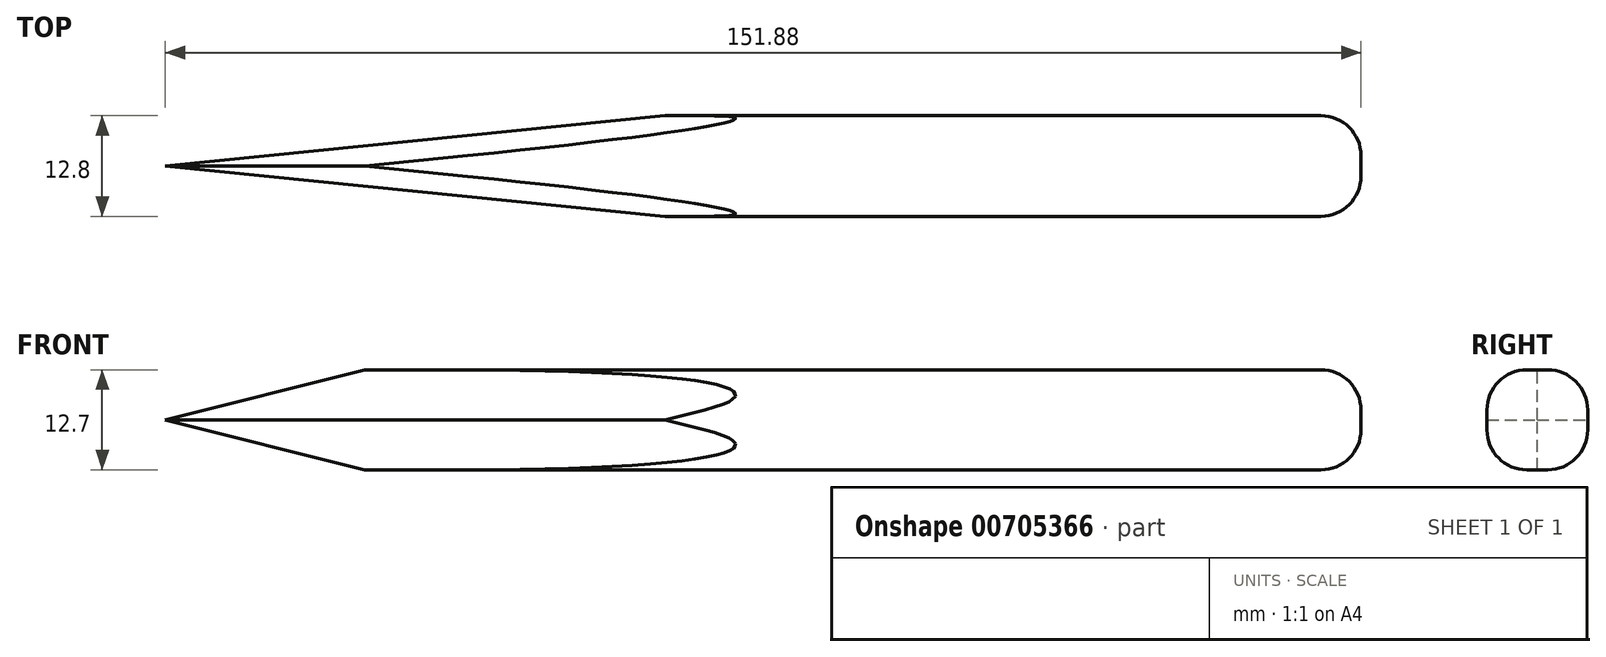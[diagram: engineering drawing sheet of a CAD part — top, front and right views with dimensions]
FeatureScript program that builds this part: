
annotation { "Feature Type Name" : "Feature", "Feature Type Description" : "" }
export const myFeature = defineFeature(function(context is Context, id is Id, definition is map)
    precondition{}
    {
        {
            var Q0;
            Q0=qCreatedBy(makeId("Top.planeOp"),FACE);
            var sketch = newSketch(context, id + "F0", { "sketchPlane" : qUnion([Q0])});
            skLineSegment(sketch, "E0.right", {"start": v(75.94, 6.4) * mm, "end": v(75.94, -6.4) * mm});
            skPoint(sketch, "E0.middle", {"position": v(0, 0) * mm});
            skLineSegment(sketch, "E1", {"start": v(-75.94, 0) * mm, "end": v(-12.44, -6.4) * mm});
            skLineSegment(sketch, "E2", {"start": v(-75.94, 0) * mm, "end": v(-12.44, 6.4) * mm});
            skLineSegment(sketch, "E3", {"start": v(-12.44, 6.4) * mm, "end": v(75.94, 6.4) * mm});
            skLineSegment(sketch, "E4", {"start": v(-12.44, -6.4) * mm, "end": v(75.94, -6.4) * mm});
            skSolve(sketch);
        }
        {
            var Q0;
            Q0=makeQuery(id+"F0.imprint","IMPRINT",FACE,{"disambiguationData":[TD([[makeQuery(id+"F0.imprint","IMPRINT",EDGE,{"derivedFrom":sQuery(id+"F0.wireOp",EDGE,"E0.right")}),-1.0]])]});
            extrude(context, id + "F1", {"entities" : qUnion([Q0]), "depth" : 12.7 * mm, "offsetDistance" : 25.4 * mm});
        }
        {
            var Q0;
            Q0=makeQuery(id+"F1.opExtrude","CAP_EDGE",EDGE,{"disambiguationData":[OSD([sQuery(id+"F0.wireOp",EDGE,"E1")])],"isStart":false});
            var Q1;
            Q1=makeQuery(id+"F1.opExtrude","CAP_EDGE",EDGE,{"disambiguationData":[OSD([sQuery(id+"F0.wireOp",EDGE,"E2")])],"isStart":false});
            var Q2;
            Q2=makeQuery(id+"F1.opExtrude","CAP_EDGE",EDGE,{"disambiguationData":[OSD([sQuery(id+"F0.wireOp",EDGE,"E1")])],"isStart":true});
            var Q3;
            Q3=makeQuery(id+"F1.opExtrude","CAP_EDGE",EDGE,{"disambiguationData":[OSD([sQuery(id+"F0.wireOp",EDGE,"E2")])],"isStart":true});
            chamfer(context, id + "F2", {"entities" : qUnion([Q0, Q1, Q2, Q3]), "chamferType" : ChamferType.TWO_OFFSETS, "width1" : 2.54 * mm, "oppositeDirection" : false, "width2" : 6.35 * mm, "tangentPropagation" : true});
        }
        {
            var Q0;
            Q0=makeQuery(id+"F1.opExtrude","CAP_EDGE",EDGE,{"disambiguationData":[OSD([sQuery(id+"F0.wireOp",EDGE,"E4")])],"isStart":false});
            var Q1;
            Q1=makeQuery(id+"F1.opExtrude","CAP_EDGE",EDGE,{"disambiguationData":[OSD([sQuery(id+"F0.wireOp",EDGE,"E4")])],"isStart":true});
            var Q2;
            Q2=makeQuery(id+"F1.opExtrude","SWEPT_EDGE",EDGE,{"disambiguationData":[OSD([sQuery(id+"F0.wireOp",EDGE,"E0.right"),sQuery(id+"F0.wireOp",EDGE,"E4")])]});
            var Q3;
            Q3=makeQuery(id+"F1.opExtrude","SWEPT_EDGE",EDGE,{"disambiguationData":[OSD([sQuery(id+"F0.wireOp",EDGE,"E0.right"),sQuery(id+"F0.wireOp",EDGE,"E3")])]});
            var Q4;
            Q4=makeQuery(id+"F1.opExtrude","CAP_EDGE",EDGE,{"disambiguationData":[OSD([sQuery(id+"F0.wireOp",EDGE,"E3")])],"isStart":false});
            var Q5;
            Q5=makeQuery(id+"F1.opExtrude","CAP_EDGE",EDGE,{"disambiguationData":[OSD([sQuery(id+"F0.wireOp",EDGE,"E0.right")])],"isStart":false});
            var Q6;
            Q6=makeQuery(id+"F1.opExtrude","CAP_EDGE",EDGE,{"disambiguationData":[OSD([sQuery(id+"F0.wireOp",EDGE,"E0.right")])],"isStart":true});
            var Q7;
            Q7=makeQuery(id+"F1.opExtrude","CAP_EDGE",EDGE,{"disambiguationData":[OSD([sQuery(id+"F0.wireOp",EDGE,"E3")])],"isStart":true});
            fillet(context, id + "F3", {"entities" : qUnion([Q0, Q1, Q2, Q3, Q4, Q5, Q6, Q7]), "radius" : 5.08 * mm, "tangentPropagation" : true, "allowEdgeOverflow" : false});
        }
    });
